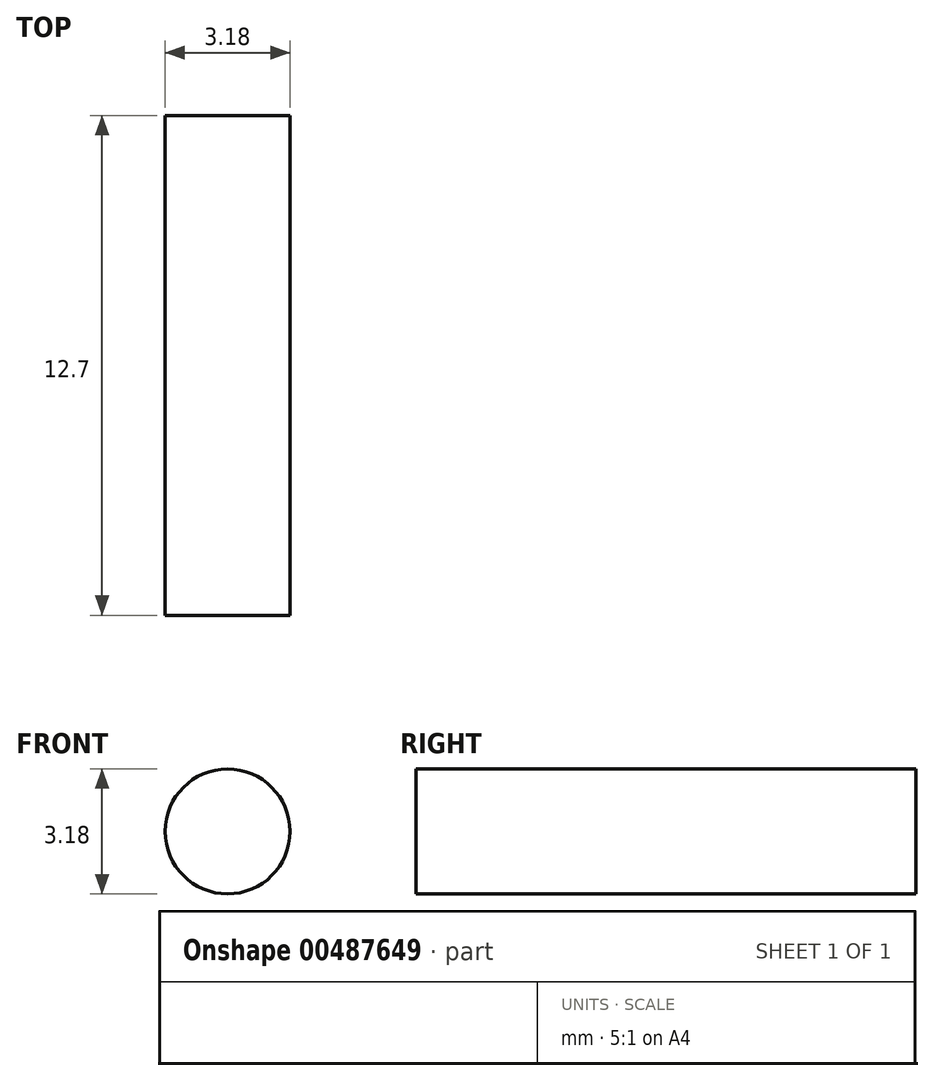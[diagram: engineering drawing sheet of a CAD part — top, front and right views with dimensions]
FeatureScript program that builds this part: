
annotation { "Feature Type Name" : "Feature", "Feature Type Description" : "" }
export const myFeature = defineFeature(function(context is Context, id is Id, definition is map)
    precondition{}
    {
        {
            var Q0;
            Q0=qCreatedBy(makeId("Front.planeOp"),FACE);
            var sketch = newSketch(context, id + "F0", { "sketchPlane" : qUnion([Q0])});
            skCircle(sketch, "E0", {"center": v(0, 0) * mm, "radius": 1.59 * mm});
            skSolve(sketch);
        }
        {
            var Q0;
            Q0 = qSketchRegion(id + "F0", true);
            extrude(context, id + "F1", {"entities" : qUnion([Q0]), "depth" : 12.7 * mm, "offsetDistance" : 25.4 * mm});
        }
    });
